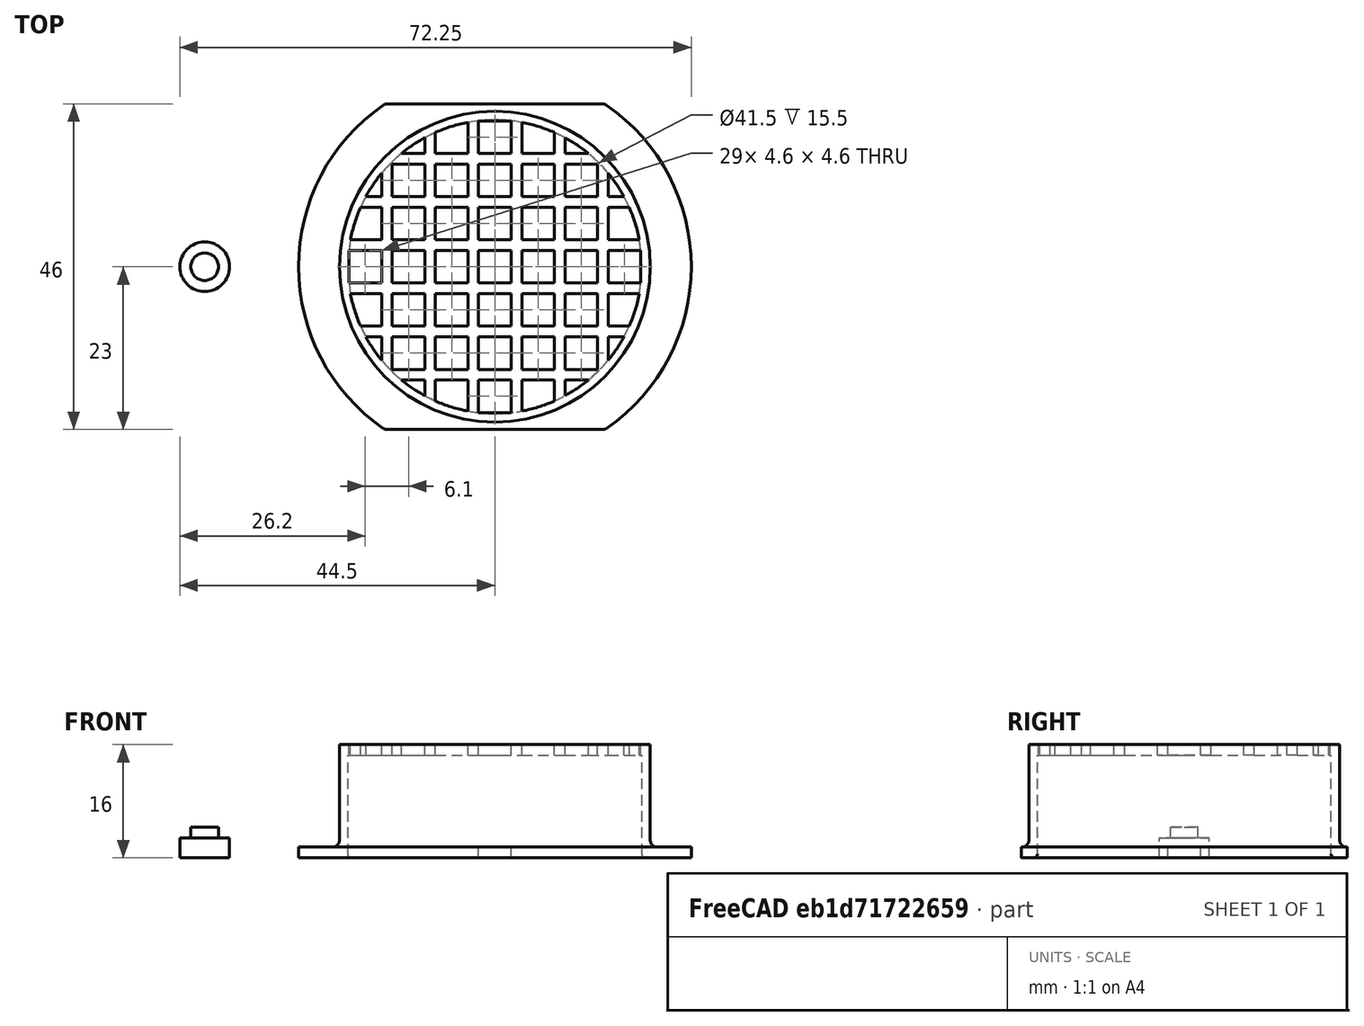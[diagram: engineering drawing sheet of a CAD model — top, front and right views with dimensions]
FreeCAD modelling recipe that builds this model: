
FCSTD DOCUMENT  (FreeCAD 0.18.4R)
Label: yuval_rejilla
License: All rights reserved
LicenseURL: http://en.wikipedia.org/wiki/All_rights_reserved
objects: Part::Cylinder×7, Part::Cut×6, Part::Box×5, Part::MultiFuse×3, Part::Fillet×3, Mesh::Feature×2, Part::FeaturePython×1
note: 25 computed .brp shape members not serialized (recipe doc carries the construction recipe); baked Part::Feature solids carry a one-line shape summary decoded from their .brp

FEATURE [Part::Cylinder] Cylinder
  Angle = 360
  AttacherType = Attacher::AttachEngine3D
  Height = 1.5
  Radius = 27.75
FEATURE [Part::Cylinder] Cylinder001
  Angle = 360
  AttacherType = Attacher::AttachEngine3D
  Height = 16
  Radius = 21.95
FEATURE [Part::MultiFuse] Fusion
  Shapes = -> [Cylinder,Cylinder001]
FEATURE [Part::Fillet] Fillet
  Base = -> Fusion
  Edges = 1 edges r=1: [Edge4]
FEATURE [Part::Cylinder] Cylinder002
  Angle = 360
  AttacherType = Attacher::AttachEngine3D
  Height = 20
  Placement = pos=(0,0,-2) rot=(0,0,1;0rad)
  Radius = 20.75
FEATURE [Part::Cut] Cut  label="parte1"
  Base = -> Fillet
  Tool = -> Cylinder002
FEATURE [Part::Cylinder] Cylinder003
  Angle = 360
  AttacherType = Attacher::AttachEngine3D
  Height = 20
  Placement = pos=(0,0,-2) rot=(0,0,1;0rad)
  Radius = 20.95
FEATURE [Part::Cylinder] Cylinder004
  Angle = 360
  AttacherType = Attacher::AttachEngine3D
  Height = 20
  Placement = pos=(0,0,-2) rot=(0,0,1;0rad)
  Radius = 35
FEATURE [Part::Cut] Cut001  label="corte_cilindro"
  Base = -> Cylinder004
  Tool = -> Cylinder003
FEATURE [Part::Box] Box  label="Cube"
  AttacherType = Attacher::AttachEngine3D
  Height = 1.5
  Length = 4.6
  Placement = pos=(-2.3,-2.3,0) rot=(0,0,1;0rad)
  Width = 4.6
FEATURE [Part::FeaturePython] Array  # Draft array (typed FeaturePython)
  Angle = 360
  ArrayType = 0
  Axis = (0,0,1)
  Base = -> Box
  Center = (0,0,0)
  Fuse = false
  IntervalAxis = (0,0,0)
  IntervalX = (6.1,0,0)
  IntervalY = (0,6.1,0)
  IntervalZ = (0,0,1)
  NumberPolar = 1
  NumberX = 7
  NumberY = 7
  NumberZ = 1
  Placement = pos=(-18.3,-18.3,0) rot=(0,0,1;0rad)
FEATURE [Part::Box] Box001  label="Cube001"
  AttacherType = Attacher::AttachEngine3D
  Height = 1.5
  Length = 4.6
  Placement = pos=(-2.3,-2.3,0) rot=(0,0,1;0rad)
  Width = 4.6
FEATURE [Part::Box] Box002  label="Cube002"
  AttacherType = Attacher::AttachEngine3D
  Height = 1.5
  Length = 45
  Placement = pos=(-22.6,-22.6,0) rot=(0,0,1;0rad)
  Width = 45
FEATURE [Part::Cut] Cut002
  Base = -> Box002
  Tool = -> Array
FEATURE [Part::Cut] Cut003  label="rejilla"
  Base = -> Cut002
  Placement = pos=(0,0,14.5) rot=(0,0,1;0rad)
  Tool = -> Cut001
FEATURE [Part::Box] Box003  label="Cube003"
  AttacherType = Attacher::AttachEngine3D
  Height = 10
  Length = 100
  Placement = pos=(-50,23,0) rot=(0,0,1;0rad)
  Width = 30
FEATURE [Part::Box] Box004  label="Cube004"
  AttacherType = Attacher::AttachEngine3D
  Height = 10
  Length = 100
  Placement = pos=(-50,-53,0) rot=(0,0,1;0rad)
  Width = 30
FEATURE [Part::MultiFuse] Fusion001
  Shapes = -> [Cut,Cut003]
FEATURE [Part::Cut] Cut004
  Base = -> Fusion001
  Tool = -> Box003
FEATURE [Part::Cut] Cut005
  Base = -> Cut004
  Tool = -> Box004
FEATURE [Part::Fillet] Fillet001
  Base = -> Cut005
  Edges = 4 edges r=1: [Edge8,Edge9,Edge13,Edge15]
FEATURE [Part::Fillet] Fillet002
  Base = -> Fillet001
  Edges = 1 edges r=0.5: [Edge34]
FEATURE [Mesh::Feature] Mesh  label="Fillet002 (Meshed)"
FEATURE [Part::Cylinder] Cylinder005
  Angle = 360
  AttacherType = Attacher::AttachEngine3D
  Height = 4.3
  Radius = 1.95
FEATURE [Part::Cylinder] Cylinder006
  Angle = 360
  AttacherType = Attacher::AttachEngine3D
  Height = 2.8
  Radius = 3.5
FEATURE [Part::MultiFuse] Fusion002  label="pituto"
  Placement = pos=(-41,0,0) rot=(0,0,1;0rad)
  Shapes = -> [Cylinder006,Cylinder005]
FEATURE [Mesh::Feature] Mesh001  label="pituto (Meshed)"
